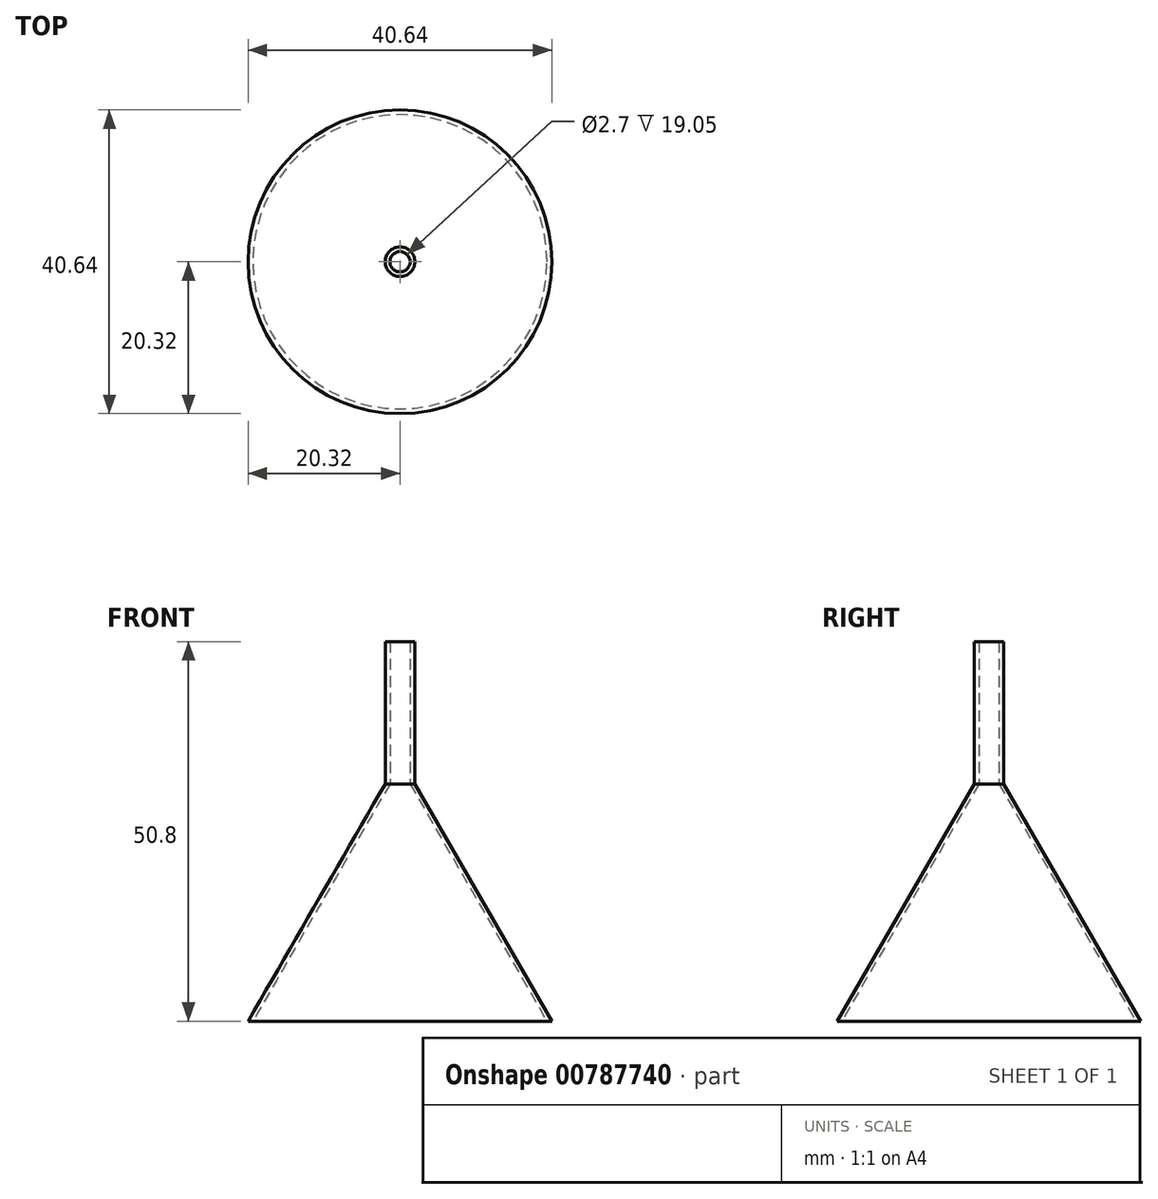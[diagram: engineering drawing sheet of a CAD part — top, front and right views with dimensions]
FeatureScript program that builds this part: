
annotation { "Feature Type Name" : "Feature", "Feature Type Description" : "" }
export const myFeature = defineFeature(function(context is Context, id is Id, definition is map)
    precondition{}
    {
        {
            var Q0;
            Q0=qCreatedBy(makeId("Front.planeOp"),FACE);
            var sketch = newSketch(context, id + "F0", { "sketchPlane" : qUnion([Q0])});
            skLineSegment(sketch, "E0", {"start": v(-1.98, 50.8) * mm, "end": v(-1.98, 31.75) * mm});
            skLineSegment(sketch, "E1", {"start": v(-1.98, 31.75) * mm, "end": v(-20.32, 0) * mm});
            skLineSegment(sketch, "E2", {"start": v(-20.32, 0) * mm, "end": v(-19.68, 0) * mm});
            skLineSegment(sketch, "E3", {"start": v(-19.68, 0) * mm, "end": v(-1.35, 31.75) * mm});
            skLineSegment(sketch, "E4", {"start": v(-1.35, 31.75) * mm, "end": v(-1.35, 50.8) * mm});
            skLineSegment(sketch, "E5", {"start": v(-1.98, 50.8) * mm, "end": v(-1.35, 50.8) * mm});
            skLineSegment(sketch, "E6", {"start": v(0, 0) * mm, "end": v(0, 51.04) * mm, "construction": true});
            skSolve(sketch);
        }
        {
            var Q0;
            Q0 = qSketchRegion(id + "F0", true);
            var Q1;
            Q1=sQuery(id+"F0.wireOp",EDGE,"E6");
            revolve(context, id + "F1", {"surfaceOperationType" : NewSurfaceOperationType.NEW, "entities" : qUnion([Q0]), "axis" : qUnion([Q1]), "revolveType" : RevolveType.FULL});
        }
    });
